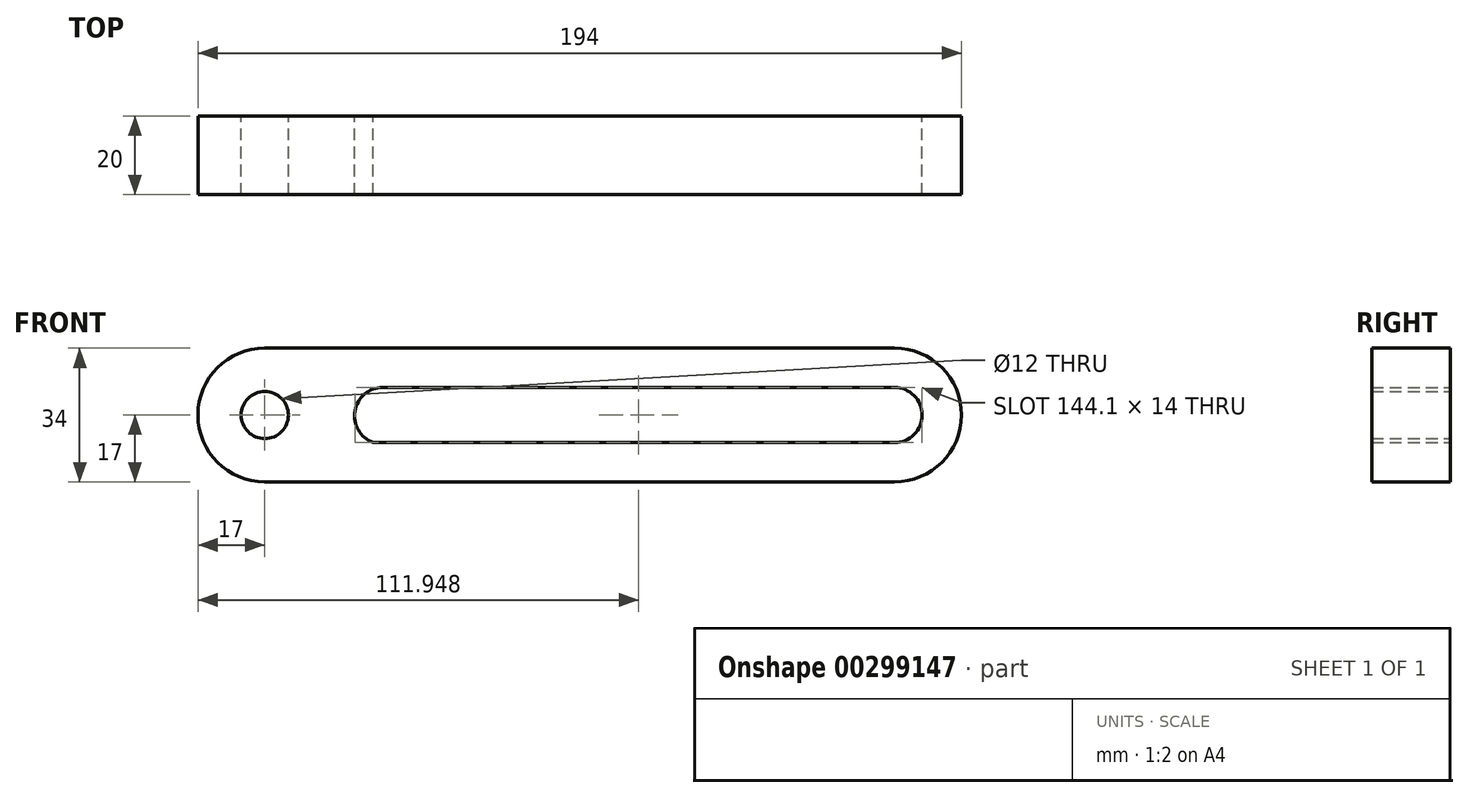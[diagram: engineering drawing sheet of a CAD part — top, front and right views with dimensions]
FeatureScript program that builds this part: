
annotation { "Feature Type Name" : "Feature", "Feature Type Description" : "" }
export const myFeature = defineFeature(function(context is Context, id is Id, definition is map)
    precondition{}
    {
        {
            var Q0;
            Q0=qCreatedBy(makeId("Front.planeOp"),FACE);
            var sketch = newSketch(context, id + "F0", { "sketchPlane" : qUnion([Q0])});
            skLineSegment(sketch, "E0", {"start": v(0, 34) * mm, "end": v(160, 34) * mm});
            skLineSegment(sketch, "E1", {"start": v(0, 0) * mm, "end": v(160, 0) * mm});
            skArc(sketch, "E2", {"start": v(0, 34) * mm, "mid": v(-17, 17) * mm, "end": v(0, 0) * mm});
            skArc(sketch, "E3", {"start": v(160, 34) * mm, "mid": v(177, 17) * mm, "end": v(160, 0) * mm});
            skCircle(sketch, "E4", {"center": v(0, 17) * mm, "radius": 6 * mm});
            skLineSegment(sketch, "E5", {"start": v(30, 24) * mm, "end": v(160, 24) * mm});
            skLineSegment(sketch, "E6", {"start": v(27.57, 10) * mm, "end": v(160, 10) * mm});
            skArc(sketch, "E7", {"start": v(160, 24) * mm, "mid": v(167, 17) * mm, "end": v(160, 10) * mm});
            skArc(sketch, "E8", {"start": v(30, 24) * mm, "mid": v(22.9, 18.02) * mm, "end": v(27.57, 10) * mm});
            skSolve(sketch);
        }
        {
            var Q0;
            Q0 = qSketchRegion(id + "F0", true);
            extrude(context, id + "F1", {"entities" : qUnion([Q0]), "depth" : 20 * mm});
        }
    });
